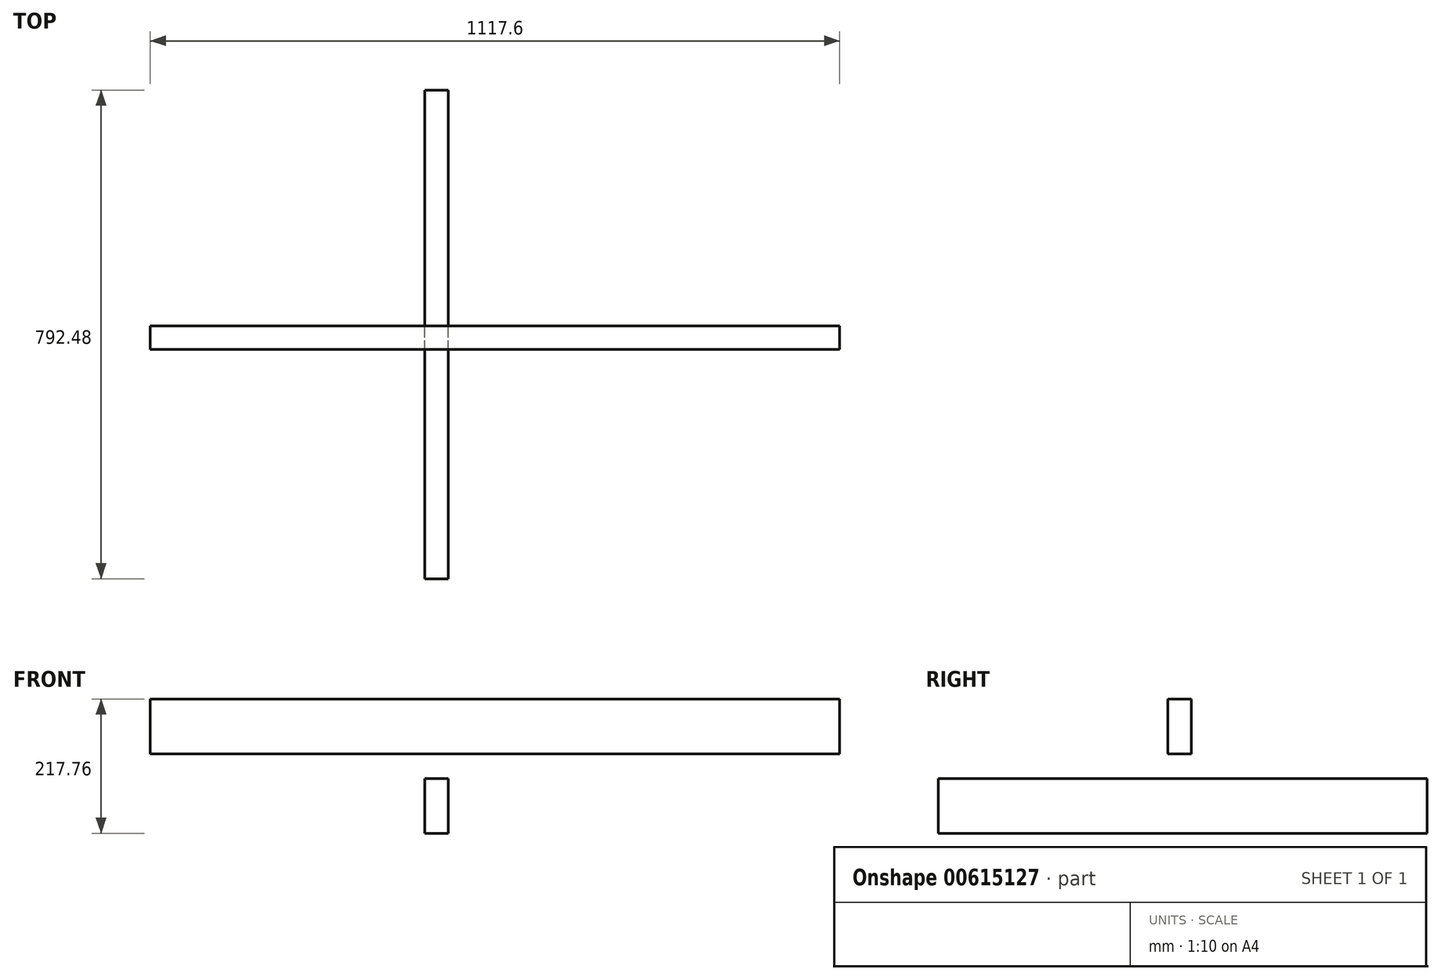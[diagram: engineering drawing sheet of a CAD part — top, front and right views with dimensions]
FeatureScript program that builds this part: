
annotation { "Feature Type Name" : "Feature", "Feature Type Description" : "" }
export const myFeature = defineFeature(function(context is Context, id is Id, definition is map)
    precondition{}
    {
        {
            var Q0;
            Q0=qCreatedBy(makeId("Front.planeOp"),FACE);
            var sketch = newSketch(context, id + "F0", { "sketchPlane" : qUnion([Q0])});
            skLineSegment(sketch, "E0.bottom", {"start": v(-444.5, 69.24) * mm, "end": v(673.1, 69.24) * mm});
            skLineSegment(sketch, "E0.top", {"start": v(-444.5, -19.66) * mm, "end": v(673.1, -19.66) * mm});
            skLineSegment(sketch, "E0.left", {"start": v(-444.5, 69.24) * mm, "end": v(-444.5, -19.66) * mm});
            skLineSegment(sketch, "E0.right", {"start": v(673.1, 69.24) * mm, "end": v(673.1, -19.66) * mm});
            skSolve(sketch);
        }
        {
            var Q0;
            Q0=makeQuery(id+"F0.imprint","IMPRINT",FACE,{"disambiguationData":[TD([[makeQuery(id+"F0.imprint","IMPRINT",EDGE,{"derivedFrom":sQuery(id+"F0.wireOp",EDGE,"E0.bottom")}),-1.0]])]});
            extrude(context, id + "F1", {"entities" : qUnion([Q0]), "depth" : 38.1 * mm});
        }
        {
            var Q0;
            Q0=qCreatedBy(makeId("Right.planeOp"),FACE);
            var sketch = newSketch(context, id + "F2", { "sketchPlane" : qUnion([Q0])});
            skLineSegment(sketch, "E1.bottom", {"start": v(-409.68, -59.62) * mm, "end": v(382.8, -59.62) * mm});
            skLineSegment(sketch, "E1.top", {"start": v(-409.68, -148.52) * mm, "end": v(382.8, -148.52) * mm});
            skLineSegment(sketch, "E1.left", {"start": v(-409.68, -59.62) * mm, "end": v(-409.68, -148.52) * mm});
            skLineSegment(sketch, "E1.right", {"start": v(382.8, -59.62) * mm, "end": v(382.8, -148.52) * mm});
            skSolve(sketch);
        }
        {
            var Q0;
            Q0=qSketchRegion(id+"F2",true);
            extrude(context, id + "F3", {"entities" : qUnion([Q0]), "depth" : 38.1 * mm});
        }
    });
